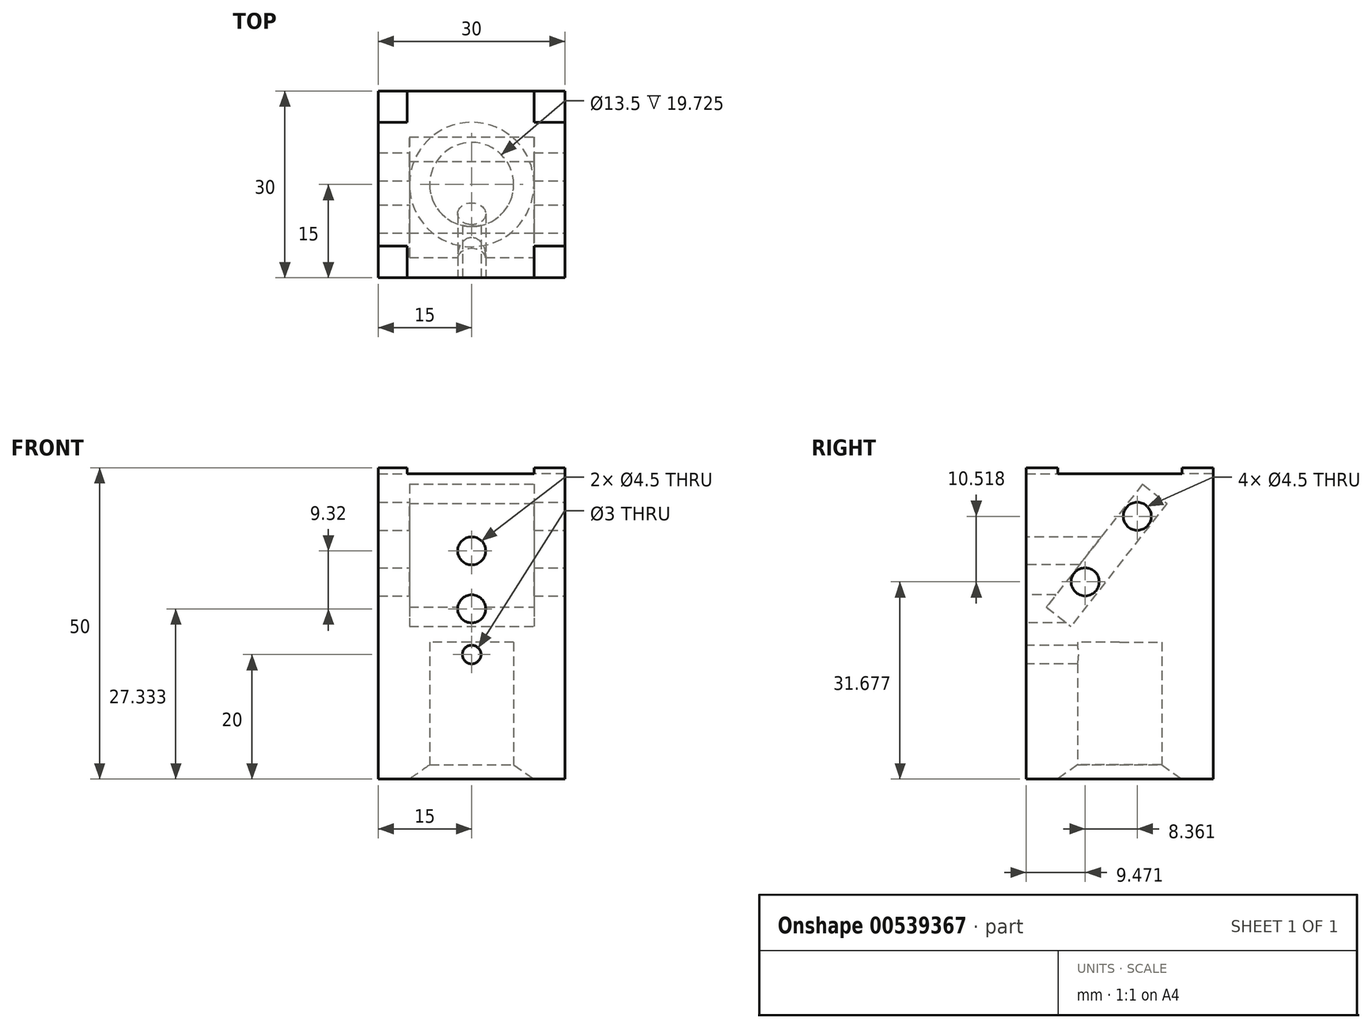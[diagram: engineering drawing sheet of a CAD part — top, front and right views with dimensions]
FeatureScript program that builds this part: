
annotation { "Feature Type Name" : "Feature", "Feature Type Description" : "" }
export const myFeature = defineFeature(function(context is Context, id is Id, definition is map)
    precondition{}
    {
        {
            var Q0;
            Q0=qCreatedBy(makeId("Top.planeOp"),FACE);
            var sketch = newSketch(context, id + "F0", { "sketchPlane" : qUnion([Q0])});
            skLineSegment(sketch, "E0.bottom", {"start": v(-15, 15) * mm, "end": v(15, 15) * mm});
            skLineSegment(sketch, "E0.top", {"start": v(-15, -15) * mm, "end": v(15, -15) * mm});
            skLineSegment(sketch, "E0.left", {"start": v(-15, 15) * mm, "end": v(-15, -15) * mm});
            skLineSegment(sketch, "E0.right", {"start": v(15, 15) * mm, "end": v(15, -15) * mm});
            skSolve(sketch);
        }
        {
            var Q0;
            Q0 = qSketchRegion(id + "F0", true);
            extrude(context, id + "F1", {"entities" : qUnion([Q0]), "depth" : 42 * mm, "offsetDistance" : 25 * mm, "hasSecondDirection" : true, "secondDirectionOppositeDirection" : true, "secondDirectionDepth" : 7 * mm});
        }
        {
            var Q0;
            Q0=qCreatedBy(makeId("Top.planeOp"),FACE);
            var sketch = newSketch(context, id + "F2", { "sketchPlane" : qUnion([Q0])});
            skCircle(sketch, "E1", {"center": v(0, 0) * mm, "radius": 6.75 * mm});
            skSolve(sketch);
        }
        {
            var Q0;
            Q0 = qSketchRegion(id + "F2", true);
            extrude(context, id + "F3", {"entities" : qUnion([Q0]), "operationType" : NewBodyOperationType.REMOVE, "depth" : 15 * mm, "offsetDistance" : 25 * mm, "hasSecondDirection" : true, "secondDirectionOppositeDirection" : true, "secondDirectionDepth" : 7 * mm});
        }
        {
            var Q0;
            Q0=qCreatedBy(makeId("Right.planeOp"),FACE);
            var sketch = newSketch(context, id + "F4", { "sketchPlane" : qUnion([Q0])});
            skLineSegment(sketch, "E2", {"start": v(-21.52, 0) * mm, "end": v(17.83, 50.36) * mm});
            skSolve(sketch);
        }
        {
            var Q0;
            Q0=sQuery(id+"F4.wireOp",EDGE,"E2");
            var Q1;
            Q1=qCreatedBy(makeId("Top.planeOp"),FACE);
            cPlane(context, id + "F5", {"entities" : qUnion([Q0, Q1]), "cplaneType" : CPlaneType.LINE_ANGLE, "offset" : 25 * mm, "angle" : 0 * degree, "width" : 150 * mm, "height" : 150 * mm});
        }
        {
            var Q0;
            Q0=qCreatedBy(id+"F5.planeOp",FACE);
            var sketch = newSketch(context, id + "F6", { "sketchPlane" : qUnion([Q0])});
            skLineSegment(sketch, "E3.bottom", {"start": v(10, 34.07) * mm, "end": v(-10, 34.07) * mm});
            skLineSegment(sketch, "E3.top", {"start": v(10, 9) * mm, "end": v(-10, 9) * mm});
            skLineSegment(sketch, "E3.left", {"start": v(10, 34.07) * mm, "end": v(10, 9) * mm});
            skLineSegment(sketch, "E3.right", {"start": v(-10, 34.07) * mm, "end": v(-10, 9) * mm});
            skSolve(sketch);
        }
        {
            var Q0;
            Q0 = qSketchRegion(id + "F6", true);
            extrude(context, id + "F7", {"entities" : qUnion([Q0]), "operationType" : NewBodyOperationType.REMOVE, "oppositeDirection" : true, "depth" : 5 * mm, "offsetDistance" : 25 * mm});
        }
        {
            var Q0;
            Q0=qCreatedBy(makeId("Right.planeOp"),FACE);
            cPlane(context, id + "F8", {"entities" : qUnion([Q0]), "cplaneType" : CPlaneType.OFFSET, "offset" : 15 * mm, "width" : 150 * mm, "height" : 150 * mm});
        }
        {
            var Q0;
            Q0=qCreatedBy(id+"F8.planeOp",FACE);
            var sketch = newSketch(context, id + "F9", { "sketchPlane" : qUnion([Q0])});
            skCircle(sketch, "E4", {"center": v(-5.53, 24.68) * mm, "radius": 2.25 * mm});
            skCircle(sketch, "E5", {"center": v(2.83, 35.2) * mm, "radius": 2.25 * mm});
            skSolve(sketch);
        }
        {
            var Q0;
            Q0 = qSketchRegion(id + "F9", true);
            extrude(context, id + "F10", {"entities" : qUnion([Q0]), "operationType" : NewBodyOperationType.REMOVE, "oppositeDirection" : true, "depth" : 50 * mm, "offsetDistance" : 25 * mm});
        }
        {
            var Q0;
            Q0=qCreatedBy(makeId("Front.planeOp"),FACE);
            cPlane(context, id + "F11", {"entities" : qUnion([Q0]), "cplaneType" : CPlaneType.OFFSET, "offset" : 15 * mm, "width" : 150 * mm, "height" : 150 * mm});
        }
        {
            var Q0;
            Q0=qCreatedBy(id+"F11.planeOp",FACE);
            var sketch = newSketch(context, id + "F12", { "sketchPlane" : qUnion([Q0])});
            skCircle(sketch, "E6", {"center": v(0, 20.33) * mm, "radius": 2.25 * mm});
            skSolve(sketch);
        }
        {
            var Q0;
            Q0 = qSketchRegion(id + "F12", true);
            extrude(context, id + "F13", {"entities" : qUnion([Q0]), "operationType" : NewBodyOperationType.REMOVE, "oppositeDirection" : true, "depth" : 7 * mm, "offsetDistance" : 25 * mm});
        }
        {
            var Q0;
            Q0=qCreatedBy(id+"F11.planeOp",FACE);
            var sketch = newSketch(context, id + "F14", { "sketchPlane" : qUnion([Q0])});
            skCircle(sketch, "E7", {"center": v(0, 29.65) * mm, "radius": 2.25 * mm});
            skSolve(sketch);
        }
        {
            var Q0;
            Q0 = qSketchRegion(id + "F14", true);
            extrude(context, id + "F15", {"entities" : qUnion([Q0]), "operationType" : NewBodyOperationType.REMOVE, "oppositeDirection" : true, "depth" : 14 * mm, "offsetDistance" : 25 * mm});
        }
        {
            var Q0;
            Q0=makeQuery(id+"F1.opExtrude","CAP_FACE",FACE,{"disambiguationData":[OSD([sQuery(id+"F0.wireOp",EDGE,"E0.bottom"),sQuery(id+"F0.wireOp",EDGE,"E0.top"),sQuery(id+"F0.wireOp",EDGE,"E0.left"),sQuery(id+"F0.wireOp",EDGE,"E0.right")])],"isStart":false});
            var sketch = newSketch(context, id + "F16", { "sketchPlane" : qUnion([Q0])});
            skLineSegment(sketch, "E8.bottom", {"start": v(15, 15) * mm, "end": v(10, 15) * mm});
            skLineSegment(sketch, "E8.top", {"start": v(15, 10) * mm, "end": v(10, 10) * mm});
            skLineSegment(sketch, "E8.left", {"start": v(15, 15) * mm, "end": v(15, 10) * mm});
            skLineSegment(sketch, "E8.right", {"start": v(10, 15) * mm, "end": v(10, 10) * mm});
            skLineSegment(sketch, "E9.bottom", {"start": v(15, -15) * mm, "end": v(10, -15) * mm});
            skLineSegment(sketch, "E9.top", {"start": v(15, -9.92) * mm, "end": v(10, -9.92) * mm});
            skLineSegment(sketch, "E9.left", {"start": v(15, -15) * mm, "end": v(15, -9.92) * mm});
            skLineSegment(sketch, "E9.right", {"start": v(10, -15) * mm, "end": v(10, -9.92) * mm});
            skLineSegment(sketch, "E10.bottom", {"start": v(-15, -15) * mm, "end": v(-10.38, -15) * mm});
            skLineSegment(sketch, "E10.top", {"start": v(-15, -9.92) * mm, "end": v(-10.38, -9.92) * mm});
            skLineSegment(sketch, "E10.left", {"start": v(-15, -15) * mm, "end": v(-15, -9.92) * mm});
            skLineSegment(sketch, "E10.right", {"start": v(-10.38, -15) * mm, "end": v(-10.38, -9.92) * mm});
            skLineSegment(sketch, "E11.bottom", {"start": v(-15, 15) * mm, "end": v(-10.38, 15) * mm});
            skLineSegment(sketch, "E11.top", {"start": v(-15, 10) * mm, "end": v(-10.38, 10) * mm});
            skLineSegment(sketch, "E11.left", {"start": v(-15, 15) * mm, "end": v(-15, 10) * mm});
            skLineSegment(sketch, "E11.right", {"start": v(-10.38, 15) * mm, "end": v(-10.38, 10) * mm});
            skSolve(sketch);
        }
        {
            var Q0;
            Q0 = qSketchRegion(id + "F16", true);
            extrude(context, id + "F17", {"entities" : qUnion([Q0]), "operationType" : NewBodyOperationType.ADD, "depth" : 1 * mm, "offsetDistance" : 25 * mm});
        }
        {
            var Q0;
            Q0=makeQuery(id+"F17.boolean.opBoolean","MERGE",FACE,{"derivedFrom":[makeQuery(id+"F1.opExtrude","SWEPT_FACE",FACE,{"disambiguationData":[OSD([sQuery(id+"F0.wireOp",EDGE,"E0.top")])]}),makeQuery(id+"F17.opExtrude","SWEPT_FACE",FACE,{"disambiguationData":[OSD([sQuery(id+"F16.wireOp",EDGE,"E9.bottom")])]}),makeQuery(id+"F17.opExtrude","SWEPT_FACE",FACE,{"disambiguationData":[OSD([sQuery(id+"F16.wireOp",EDGE,"E10.bottom")])]})]});
            var sketch = newSketch(context, id + "F18", { "sketchPlane" : qUnion([Q0])});
            skCircle(sketch, "E12", {"center": v(0, 13) * mm, "radius": 1.5 * mm});
            skSolve(sketch);
        }
        {
            var Q0;
            Q0 = qSketchRegion(id + "F18", true);
            extrude(context, id + "F19", {"entities" : qUnion([Q0]), "operationType" : NewBodyOperationType.REMOVE, "endBound" : BoundingType.UP_TO_NEXT, "oppositeDirection" : true, "depth" : 25 * mm, "offsetDistance" : 25 * mm});
        }
        {
            var Q0;
            Q0=qCreatedBy(makeId("Right.planeOp"),FACE);
            var sketch = newSketch(context, id + "F20", { "sketchPlane" : qUnion([Q0])});
            skLineSegment(sketch, "E13", {"start": v(0, 0) * mm, "end": v(0, -7) * mm});
            skLineSegment(sketch, "E14", {"start": v(0, -7) * mm, "end": v(-10, -7) * mm});
            skLineSegment(sketch, "E15", {"start": v(-10, -7) * mm, "end": v(0, 0) * mm});
            skSolve(sketch);
        }
        {
            var Q0;
            Q0 = qSketchRegion(id + "F20", true);
            var Q1;
            Q1=sQuery(id+"F20.wireOp",EDGE,"E13");
            revolve(context, id + "F21", {"operationType" : NewBodyOperationType.REMOVE, "surfaceOperationType" : NewSurfaceOperationType.NEW, "entities" : qUnion([Q0]), "axis" : qUnion([Q1]), "revolveType" : RevolveType.FULL, "oppositeDirection" : true});
        }
    });
